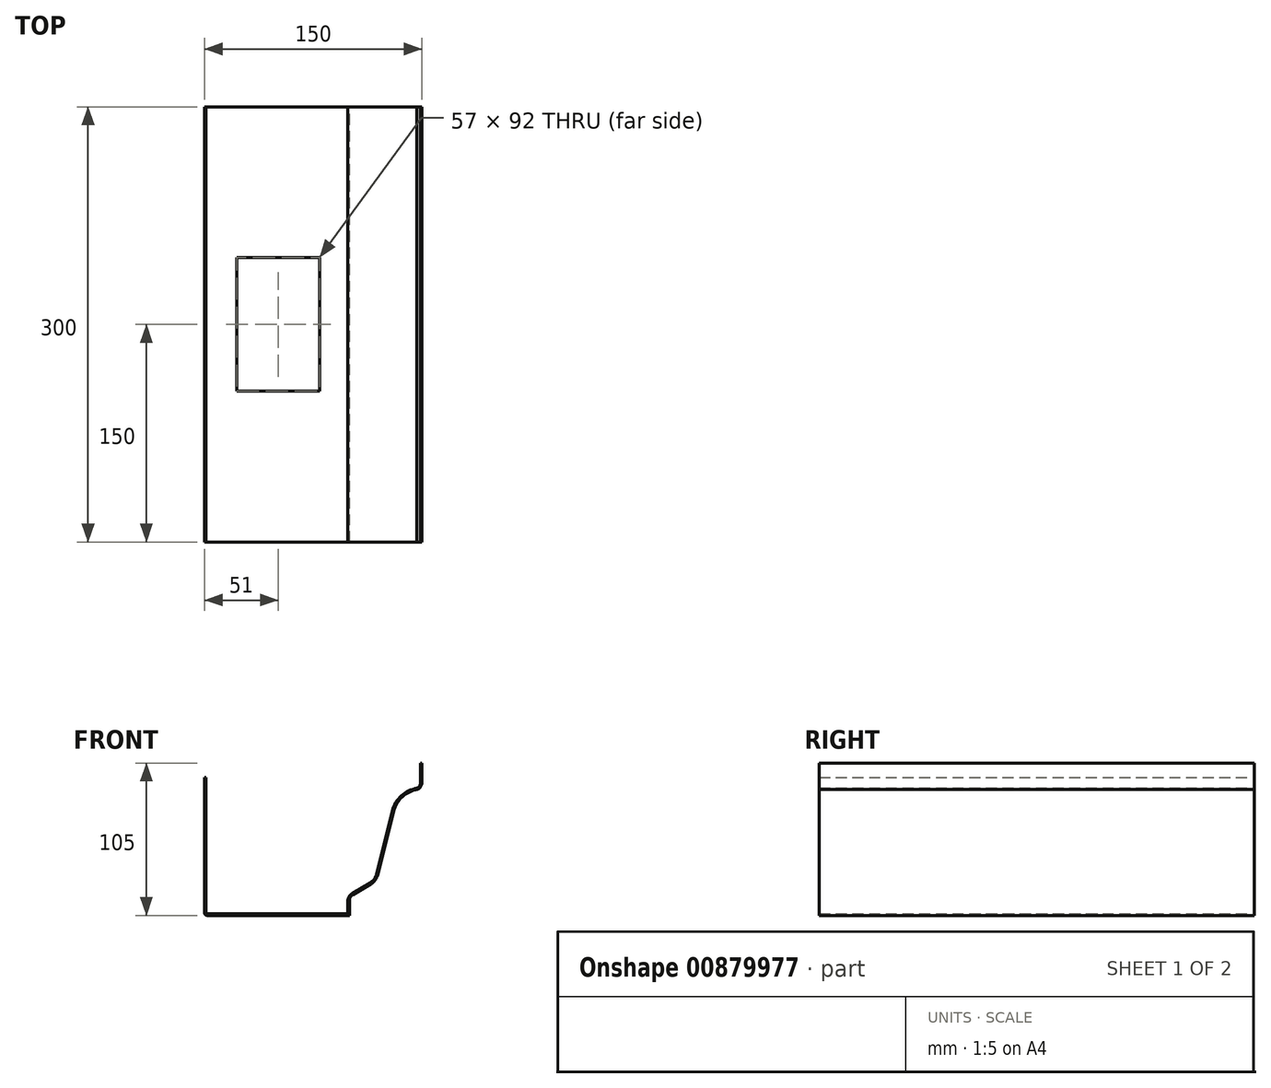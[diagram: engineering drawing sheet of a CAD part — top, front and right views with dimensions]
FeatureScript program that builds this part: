
annotation { "Feature Type Name" : "Feature", "Feature Type Description" : "" }
export const myFeature = defineFeature(function(context is Context, id is Id, definition is map)
    precondition{}
    {
        {
            var Q0;
            Q0=qCreatedBy(makeId("Front.planeOp"),FACE);
            var sketch = newSketch(context, id + "F0", { "sketchPlane" : qUnion([Q0])});
            skLineSegment(sketch, "E0.right", {"start": v(75, 52.5) * mm, "end": v(75, 38.91) * mm});
            skPoint(sketch, "E0.middle", {"position": v(0, 0) * mm});
            skArc(sketch, "E1", {"start": v(71.93, 34.26) * mm, "mid": v(61.54, 29.3) * mm, "end": v(55.61, 19.41) * mm});
            skArc(sketch, "E2", {"start": v(39.92, -30.84) * mm, "mid": v(42.75, -28.3) * mm, "end": v(44.39, -24.88) * mm});
            skArc(sketch, "E3", {"start": v(27.46, -38.2) * mm, "mid": v(25.66, -40.02) * mm, "end": v(25, -42.5) * mm});
            skLineSegment(sketch, "E4", {"start": v(27.46, -38.2) * mm, "end": v(39.92, -30.84) * mm});
            skLineSegment(sketch, "E5", {"start": v(44.39, -24.88) * mm, "end": v(55.61, 19.41) * mm});
            skArc(sketch, "E6", {"start": v(71.93, 34.26) * mm, "mid": v(74.17, 36.12) * mm, "end": v(75, 38.91) * mm});
            skPoint(sketch, "E7.orphan", {"position": v(-75, -52.5) * mm});
            skPoint(sketch, "E8.right.start.orphan", {"position": v(25, -52.5) * mm});
            skLineSegment(sketch, "E9", {"start": v(-73, -52.5) * mm, "end": v(25, -52.5) * mm});
            skLineSegment(sketch, "E10", {"start": v(25, -52.5) * mm, "end": v(25, -42.5) * mm});
            skLineSegment(sketch, "E11", {"start": v(-75, -50.5) * mm, "end": v(-75, 42.5) * mm});
            skLineSegment(sketch, "E12", {"start": v(-74, 42.5) * mm, "end": v(-74, -50.5) * mm});
            skLineSegment(sketch, "E13", {"start": v(-73, -51.5) * mm, "end": v(24, -51.5) * mm});
            skLineSegment(sketch, "E14", {"start": v(24, -51.5) * mm, "end": v(24, -42.5) * mm});
            skLineSegment(sketch, "E15", {"start": v(26.95, -37.33) * mm, "end": v(39.41, -29.98) * mm});
            skLineSegment(sketch, "E16", {"start": v(74, 52.5) * mm, "end": v(74, 38.88) * mm});
            skLineSegment(sketch, "E17", {"start": v(74, 52.5) * mm, "end": v(75, 52.5) * mm});
            skArc(sketch, "E18.trimOffspring", {"start": v(26.95, -37.33) * mm, "mid": v(24.79, -39.52) * mm, "end": v(24, -42.5) * mm});
            skArc(sketch, "E19", {"start": v(39.41, -29.98) * mm, "mid": v(41.95, -27.7) * mm, "end": v(43.42, -24.63) * mm});
            skArc(sketch, "E20", {"start": v(71.65, 35.23) * mm, "mid": v(60.82, 29.99) * mm, "end": v(54.64, 19.66) * mm});
            skLineSegment(sketch, "E21", {"start": v(54.64, 19.66) * mm, "end": v(43.42, -24.63) * mm});
            skArc(sketch, "E22", {"start": v(71.65, 35.23) * mm, "mid": v(73.36, 36.7) * mm, "end": v(74, 38.88) * mm});
            skPoint(sketch, "E23", {"position": v(-73, -50.5) * mm});
            skArc(sketch, "E24", {"start": v(-74, -50.5) * mm, "mid": v(-73.7, -51.2) * mm, "end": v(-73, -51.5) * mm});
            skArc(sketch, "E25", {"start": v(-75, -50.5) * mm, "mid": v(-74.41, -51.91) * mm, "end": v(-73, -52.5) * mm});
            skPoint(sketch, "E26.orphan", {"position": v(-74, -51.5) * mm});
            skLineSegment(sketch, "E27", {"start": v(-75, 42.5) * mm, "end": v(-74, 42.5) * mm});
            skSolve(sketch);
        }
        {
            var Q0;
            Q0 = qSketchRegion(id + "F0", true);
            extrude(context, id + "F1", {"entities" : qUnion([Q0]), "depth" : 300 * mm, "offsetDistance" : 25 * mm});
        }
        {
            var Q0;
            Q0=makeQuery(id+"F1.opExtrude","SWEPT_FACE",FACE,{"disambiguationData":[OSD([sQuery(id+"F0.wireOp",EDGE,"E9")])]});
            var sketch = newSketch(context, id + "F2", { "sketchPlane" : qUnion([Q0])});
            skPoint(sketch, "E28", {"position": v(-24, 150) * mm});
            skPoint(sketch, "E28.positionSnap0", {"position": v(-24, 0) * mm});
            skPoint(sketch, "E28.positionSnap1", {"position": v(25, 150) * mm});
            skLineSegment(sketch, "E29.bottom", {"start": v(4.5, 104) * mm, "end": v(-52.5, 104) * mm});
            skLineSegment(sketch, "E29.top", {"start": v(4.5, 196) * mm, "end": v(-52.5, 196) * mm});
            skLineSegment(sketch, "E29.left", {"start": v(4.5, 104) * mm, "end": v(4.5, 196) * mm});
            skLineSegment(sketch, "E29.right", {"start": v(-52.5, 104) * mm, "end": v(-52.5, 196) * mm});
            skSolve(sketch);
        }
        {
            var Q0;
            Q0 = qSketchRegion(id + "F2", true);
            extrude(context, id + "F3", {"entities" : qUnion([Q0]), "operationType" : NewBodyOperationType.REMOVE, "oppositeDirection" : true, "depth" : 25 * mm, "offsetDistance" : 25 * mm});
        }
        {
            var Q0;
            Q0 = qSketchRegion(id + "F2", true);
            extrude(context, id + "F4", {"entities" : qUnion([Q0]), "operationType" : NewBodyOperationType.REMOVE, "oppositeDirection" : true, "depth" : 25 * mm, "offsetDistance" : 25 * mm});
        }
        {
            var Q0;
            Q0 = qSketchRegion(id + "F2", true);
            extrude(context, id + "F5", {"entities" : qUnion([Q0]), "operationType" : NewBodyOperationType.REMOVE, "oppositeDirection" : true, "depth" : 25 * mm, "offsetDistance" : 25 * mm});
        }
    });
